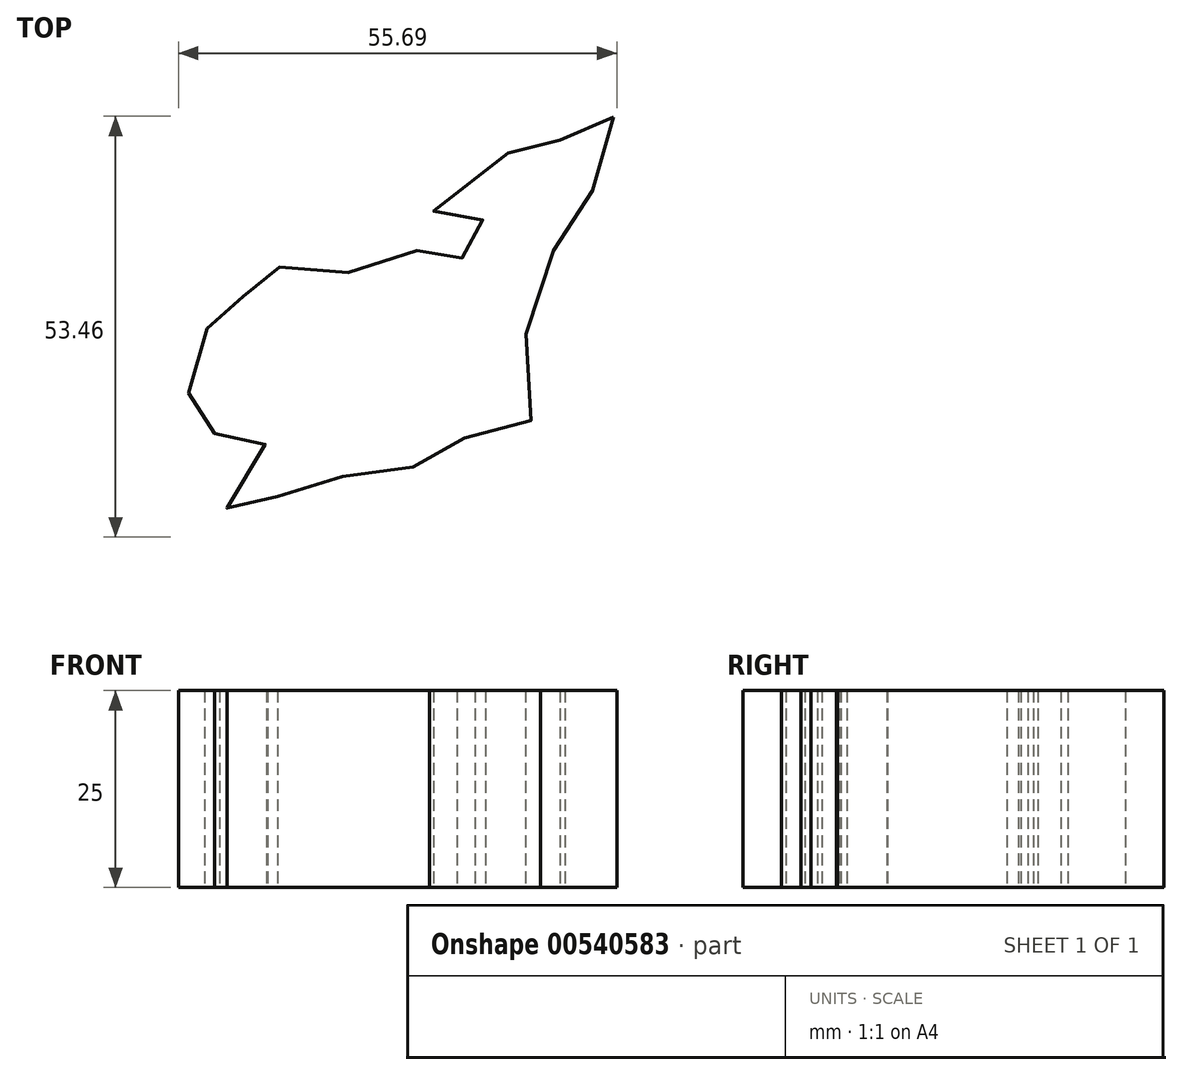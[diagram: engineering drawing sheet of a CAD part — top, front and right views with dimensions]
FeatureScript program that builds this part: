
annotation { "Feature Type Name" : "Feature", "Feature Type Description" : "" }
export const myFeature = defineFeature(function(context is Context, id is Id, definition is map)
    precondition{}
    {
        {
            var Q0;
            Q0=qCreatedBy(makeId("Top.planeOp"),FACE);
            var sketch = newSketch(context, id + "F0", { "sketchPlane" : qUnion([Q0])});
            skFitSpline(sketch, "E0", {"points": [v(19.86, 29.74) * mm, v(14.21, 26.76) * mm, v(13.27, 25.04) * mm, v(13.11, 27.07) * mm, v(13.58, 29.74) * mm, v(9.5, 27.54) * mm, v(3.07, 23.15) * mm, v(-1.79, 20.8) * mm, v(-2.73, 17.04) * mm, v(0, 17.35) * mm, v(1.82, 17.66) * mm, v(3.55, 16.88) * mm, v(0, 15.94) * mm, v(1.98, 14.53) * mm, v(1.2, 11.7) * mm, v(-1.79, 13.9) * mm, v(-2.73, 12.17) * mm, v(-4.3, 11.55) * mm, v(-5.55, 13.27) * mm, v(-7.75, 11.86) * mm, v(-11.2, 10.6) * mm, v(-16.06, 10.3) * mm, v(-18.88, 12.64) * mm, v(-21.4, 10.92) * mm, v(-24.06, 10.45) * mm, v(-22.8, 8.1) * mm, v(-26.1, 7.15) * mm, v(-28.92, 6.53) * mm, v(-32.06, 5.12) * mm, v(-30.8, 3.55) * mm, v(-32.84, 2.45) * mm, v(-34.57, 0) * mm, v(-35.04, -5.08) * mm, v(-32.22, -5.24) * mm, v(-30.96, -6.8) * mm, v(-30.18, -9.16) * mm, v(-30.8, -10.41) * mm, v(-29.4, -13.55) * mm, v(-27.35, -11.67) * mm, v(-24.37, -11.82) * mm, v(-24.69, -13.24) * mm, v(-27.67, -16.22) * mm, v(-29.24, -20.14) * mm, v(-27.35, -23.59) * mm, v(-24.37, -19.98) * mm, v(-21.24, -18.1) * mm, v(-18.41, -18.57) * mm, v(-15.43, -15.75) * mm, v(-13.4, -16.22) * mm, v(-10.57, -14.18) * mm, v(-6.8, -14.96) * mm, v(-3.51, -12.6) * mm, v(-3.51, -11.2) * mm, v(0, -11.67) * mm, v(1.66, -10.41) * mm, v(4.8, -11.51) * mm, v(8.25, -10.1) * mm, v(10.6, -5.7) * mm, v(9.2, -1.79) * mm, v(9.03, 3.55) * mm, v(11.07, 7.47) * mm, v(12.02, 12.49) * mm, v(13.43, 13.59) * mm, v(15.62, 15.62) * mm, v(17.03, 19.86) * mm, v(17.98, 22.21) * mm, v(19.39, 25.04) * mm, v(19.86, 29.74) * mm]});
            skSolve(sketch);
        }
        {
            var Q0;
            Q0 = qSketchRegion(id + "F0", true);
            extrude(context, id + "F1", {"entities" : qUnion([Q0]), "depth" : 25 * mm, "offsetDistance" : 25 * mm});
        }
    });
